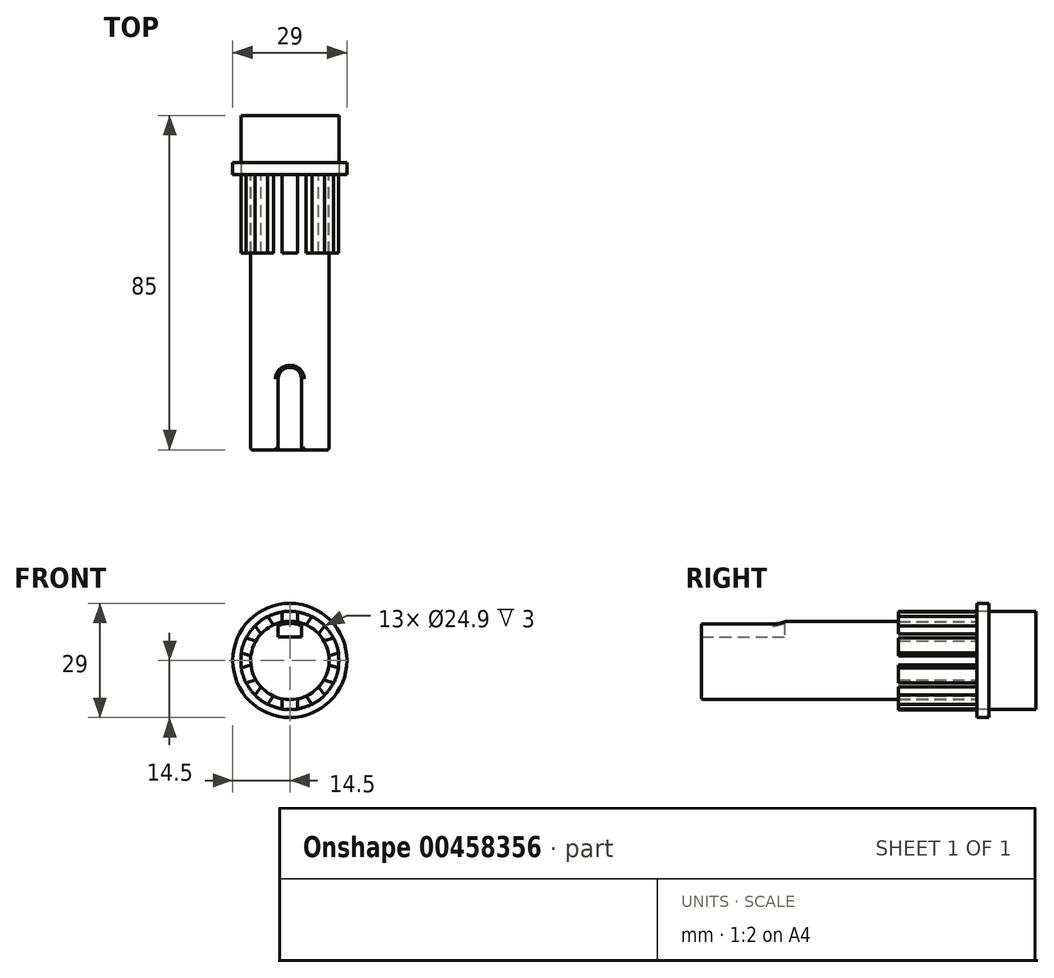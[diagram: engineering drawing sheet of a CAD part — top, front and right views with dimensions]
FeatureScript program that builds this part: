
annotation { "Feature Type Name" : "Feature", "Feature Type Description" : "" }
export const myFeature = defineFeature(function(context is Context, id is Id, definition is map)
    precondition{}
    {
        {
            var Q0;
            Q0=qCreatedBy(makeId("Front.planeOp"),FACE);
            var sketch = newSketch(context, id + "F0", { "sketchPlane" : qUnion([Q0])});
            skCircle(sketch, "E0", {"center": v(0, 0) * mm, "radius": 14.5 * mm});
            skCircle(sketch, "E1", {"center": v(0, 0) * mm, "radius": 12.45 * mm});
            skCircle(sketch, "E2", {"center": v(0, 0) * mm, "radius": 9.95 * mm});
            skSolve(sketch);
        }
        {
            var Q0;
            Q0=makeQuery(id+"F0.imprint","IMPRINT",FACE,{"disambiguationData":[TD([[makeQuery(id+"F0.imprint","IMPRINT",EDGE,{"derivedFrom":sQuery(id+"F0.wireOp",EDGE,"E1")}),1.0]])]});
            var Q1;
            Q1=makeQuery(id+"F0.imprint","IMPRINT",FACE,{"disambiguationData":[TD([[makeQuery(id+"F0.imprint","IMPRINT",EDGE,{"derivedFrom":sQuery(id+"F0.wireOp",EDGE,"E2")}),1.0]])]});
            extrude(context, id + "F1", {"entities" : qUnion([Q0, Q1]), "oppositeDirection" : true, "depth" : 15 * mm});
        }
        {
            var Q0;
            Q0=makeQuery(id+"F0.imprint","IMPRINT",FACE,{"disambiguationData":[TD([[makeQuery(id+"F0.imprint","IMPRINT",EDGE,{"derivedFrom":sQuery(id+"F0.wireOp",EDGE,"E2")}),1.0]])]});
            extrude(context, id + "F2", {"entities" : qUnion([Q0]), "operationType" : NewBodyOperationType.ADD, "depth" : 70 * mm});
        }
        {
            var Q0;
            Q0=makeQuery(id+"F0.imprint","IMPRINT",FACE,{"disambiguationData":[TD([[makeQuery(id+"F0.imprint","IMPRINT",EDGE,{"derivedFrom":sQuery(id+"F0.wireOp",EDGE,"E0")}),1.0]])]});
            extrude(context, id + "F3", {"entities" : qUnion([Q0]), "oppositeDirection" : true, "depth" : 3 * mm});
        }
        {
            var Q0;
            Q0=qCreatedBy(makeId("Front.planeOp"),FACE);
            var sketch = newSketch(context, id + "F4", { "sketchPlane" : qUnion([Q0])});
            skLineSegment(sketch, "E3.left", {"start": v(2, 12.34) * mm, "end": v(2, 9.75) * mm});
            skLineSegment(sketch, "E3.right", {"start": v(-2, 12.34) * mm, "end": v(-2, 9.75) * mm});
            skPoint(sketch, "E3.middle", {"position": v(0, 0) * mm});
            skPoint(sketch, "E4.orphan", {"position": v(2, 12.5) * mm});
            skPoint(sketch, "E5.orphan", {"position": v(-2, 12.5) * mm});
            skArc(sketch, "E6.trimOffspring", {"start": v(2, 12.34) * mm, "mid": v(0, 12.5) * mm, "end": v(-2, 12.34) * mm});
            skPoint(sketch, "E7.orphan", {"position": v(-2, -12.5) * mm});
            skPoint(sketch, "E8.orphan", {"position": v(2, -12.5) * mm});
            skArc(sketch, "E9.trimOffspring", {"start": v(2, 9.75) * mm, "mid": v(0, 9.95) * mm, "end": v(-2, 9.75) * mm});
            skSolve(sketch);
        }
        {
            var Q0;
            Q0 = qSketchRegion(id + "F4", true);
            extrude(context, id + "F5", {"entities" : qUnion([Q0]), "depth" : 20 * mm});
        }
        {
            var Q0;
            Q0=makeQuery(id+"F5.opExtrude","SWEPT_BODY",BODY,{"disambiguationData":[OSD([sQuery(id+"F4.wireOp",EDGE,"E3.left"),sQuery(id+"F4.wireOp",EDGE,"E3.right"),sQuery(id+"F4.wireOp",EDGE,"KaGKPjfN-YMTT-E5b1-NYma-lMDyYsubxa9v"),sQuery(id+"F4.wireOp",EDGE,"E6.trimOffspring")])]});
            var Q1;
            Q1=makeQuery(id+"F2.opExtrude","SWEPT_FACE",FACE,{"disambiguationData":[OSD([sQuery(id+"F0.wireOp",EDGE,"E2")])]});
            circularPattern(context, id + "F6", {"entities" : qUnion([Q0]), "axis" : qUnion([Q1]), "angle" : 360 * degree, "instanceCount" : 10, "equalSpace" : true});
        }
        {
            var Q0;
            Q0=qCreatedBy(makeId("Top.planeOp"),FACE);
            cPlane(context, id + "F7", {"entities" : qUnion([Q0]), "cplaneType" : CPlaneType.OFFSET, "offset" : 6 * mm, "width" : 150 * mm, "height" : 150 * mm});
        }
        {
            var Q0;
            Q0=qCreatedBy(id+"F7.planeOp",FACE);
            var sketch = newSketch(context, id + "F8", { "sketchPlane" : qUnion([Q0])});
            skLineSegment(sketch, "E10.bottom", {"start": v(-3, -70) * mm, "end": v(3, -70) * mm});
            skLineSegment(sketch, "E10.left", {"start": v(-3, -70) * mm, "end": v(-3, -52) * mm});
            skLineSegment(sketch, "E10.right", {"start": v(3, -70) * mm, "end": v(3, -52) * mm});
            skArc(sketch, "E11", {"start": v(3, -52) * mm, "mid": v(0, -49) * mm, "end": v(-3, -52) * mm});
            skPoint(sketch, "E11.first.point", {"position": v(-0.6, -54.94) * mm});
            skPoint(sketch, "E11.second.point", {"position": v(2.55, -53.58) * mm});
            skPoint(sketch, "E11.third.point", {"position": v(2.53, -50.39) * mm});
            skSolve(sketch);
        }
        {
            var Q0;
            Q0 = qSketchRegion(id + "F8", true);
            extrude(context, id + "F9", {"entities" : qUnion([Q0]), "operationType" : NewBodyOperationType.REMOVE, "depth" : 3.95 * mm});
        }
        {
            var Q0;
            Q0=makeQuery(id+"F2.opExtrude","CAP_EDGE",EDGE,{"disambiguationData":[OSD([sQuery(id+"F0.wireOp",EDGE,"E2")])],"isStart":false});
            var Q1;
            Q1=makeQuery(id+"F9.boolean.opBoolean","INTERSECT",EDGE,{"derivedFrom":[makeQuery(id+"F2.opExtrude","SWEPT_FACE",FACE,{"disambiguationData":[OSD([sQuery(id+"F0.wireOp",EDGE,"E2")])]}),makeQuery(id+"F9.opExtrude","SWEPT_FACE",FACE,{"disambiguationData":[OSD([sQuery(id+"F8.wireOp",EDGE,"E10.left")])]})]});
            var Q2;
            Q2=makeQuery(id+"F9.boolean.opBoolean","INTERSECT",EDGE,{"derivedFrom":[makeQuery(id+"F2.opExtrude","SWEPT_FACE",FACE,{"disambiguationData":[OSD([sQuery(id+"F0.wireOp",EDGE,"E2")])]}),makeQuery(id+"F9.opExtrude","SWEPT_FACE",FACE,{"disambiguationData":[OSD([sQuery(id+"F8.wireOp",EDGE,"E11")])]})]});
            var Q3;
            Q3=makeQuery(id+"F9.boolean.opBoolean","INTERSECT",EDGE,{"derivedFrom":[makeQuery(id+"F2.opExtrude","SWEPT_FACE",FACE,{"disambiguationData":[OSD([sQuery(id+"F0.wireOp",EDGE,"E2")])]}),makeQuery(id+"F9.opExtrude","SWEPT_FACE",FACE,{"disambiguationData":[OSD([sQuery(id+"F8.wireOp",EDGE,"E10.right")])]})]});
            fillet(context, id + "F10", {"entities" : qUnion([Q0, Q1, Q2, Q3]), "radius" : 0.5 * mm, "tangentPropagation" : true, "allowEdgeOverflow" : false});
        }
    });
